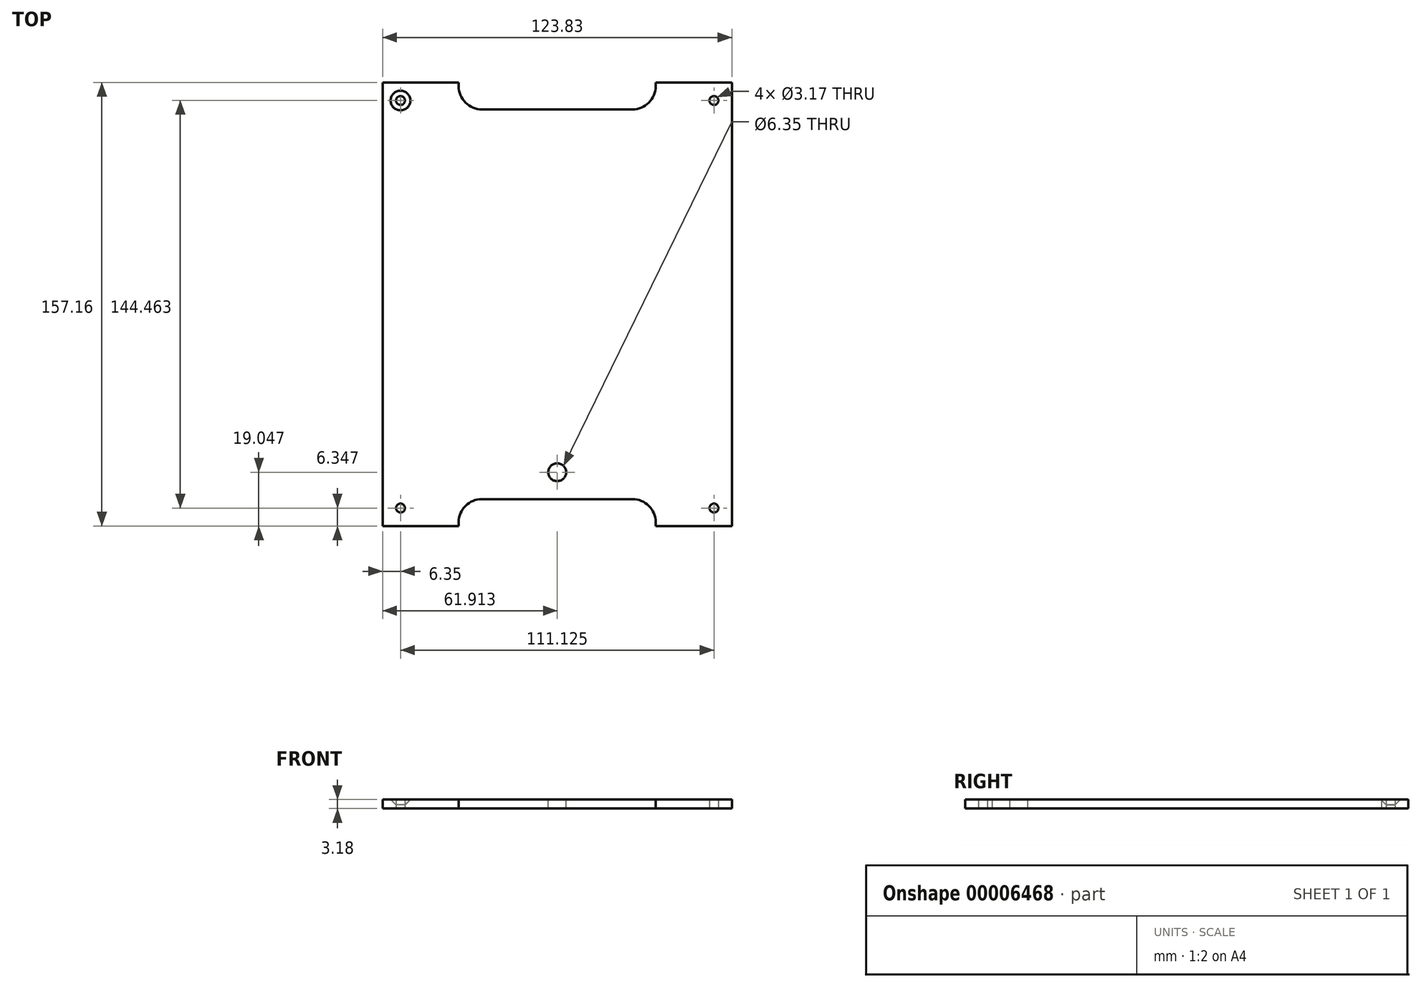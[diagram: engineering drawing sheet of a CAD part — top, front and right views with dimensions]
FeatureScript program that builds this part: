
annotation { "Feature Type Name" : "Feature", "Feature Type Description" : "" }
export const myFeature = defineFeature(function(context is Context, id is Id, definition is map)
    precondition{}
    {
        {
            var Q0;
            Q0=qCreatedBy(makeId("Top.planeOp"),FACE);
            var sketch = newSketch(context, id + "F0", { "sketchPlane" : qUnion([Q0])});
            skLineSegment(sketch, "E0.bottom", {"start": v(0, 0) * mm, "end": v(26.99, 0) * mm});
            skLineSegment(sketch, "E0.top", {"start": v(0, -157.16) * mm, "end": v(26.99, -157.16) * mm});
            skLineSegment(sketch, "E0.left", {"start": v(0, 0) * mm, "end": v(0, -157.16) * mm});
            skLineSegment(sketch, "E0.right", {"start": v(123.83, 0) * mm, "end": v(123.83, -157.16) * mm});
            skLineSegment(sketch, "E1", {"start": v(26.99, 0) * mm, "end": v(26.99, -1.27) * mm});
            skLineSegment(sketch, "E2", {"start": v(35.24, -9.53) * mm, "end": v(88.58, -9.53) * mm});
            skLineSegment(sketch, "E3", {"start": v(96.84, -1.27) * mm, "end": v(96.84, 0) * mm});
            skLineSegment(sketch, "E4", {"start": v(26.99, -157.16) * mm, "end": v(26.99, -155.9) * mm});
            skLineSegment(sketch, "E5", {"start": v(35.24, -147.64) * mm, "end": v(88.58, -147.64) * mm});
            skLineSegment(sketch, "E6", {"start": v(96.84, -155.9) * mm, "end": v(96.84, -157.16) * mm});
            skLineSegment(sketch, "E7.trimOffspring", {"start": v(96.84, 0) * mm, "end": v(123.83, 0) * mm});
            skLineSegment(sketch, "E8.trimOffspring", {"start": v(96.84, -157.16) * mm, "end": v(123.83, -157.16) * mm});
            skPoint(sketch, "E9.visualSharp", {"position": v(26.99, -9.53) * mm});
            skArc(sketch, "E9.filletArc", {"start": v(26.99, -1.27) * mm, "mid": v(29.4, -7.1) * mm, "end": v(35.24, -9.53) * mm});
            skPoint(sketch, "E10.visualSharp", {"position": v(96.84, -9.53) * mm});
            skArc(sketch, "E10.filletArc", {"start": v(88.58, -9.53) * mm, "mid": v(94.42, -7.1) * mm, "end": v(96.84, -1.27) * mm});
            skPoint(sketch, "E11.visualSharp", {"position": v(96.84, -147.64) * mm});
            skArc(sketch, "E11.filletArc", {"start": v(96.84, -155.9) * mm, "mid": v(94.42, -150.06) * mm, "end": v(88.58, -147.64) * mm});
            skPoint(sketch, "E12.visualSharp", {"position": v(26.99, -147.64) * mm});
            skArc(sketch, "E12.filletArc", {"start": v(35.24, -147.64) * mm, "mid": v(29.4, -150.06) * mm, "end": v(26.99, -155.9) * mm});
            skLineSegment(sketch, "E13.bottom", {"start": v(6.35, -6.35) * mm, "end": v(117.48, -6.35) * mm, "construction": true});
            skLineSegment(sketch, "E13.top", {"start": v(6.35, -150.81) * mm, "end": v(117.48, -150.81) * mm, "construction": true});
            skLineSegment(sketch, "E13.left", {"start": v(6.35, -6.35) * mm, "end": v(6.35, -150.81) * mm, "construction": true});
            skLineSegment(sketch, "E13.right", {"start": v(117.48, -6.35) * mm, "end": v(117.48, -150.81) * mm, "construction": true});
            skCircle(sketch, "E14", {"center": v(6.35, -6.35) * mm, "radius": 1.59 * mm});
            skCircle(sketch, "E15", {"center": v(117.48, -6.35) * mm, "radius": 1.59 * mm});
            skCircle(sketch, "E16", {"center": v(117.48, -150.81) * mm, "radius": 1.59 * mm});
            skCircle(sketch, "E17", {"center": v(6.35, -150.81) * mm, "radius": 1.59 * mm});
            skSolve(sketch);
        }
        {
            var Q0;
            Q0 = qSketchRegion(id + "F0", true);
            extrude(context, id + "F1", {"entities" : qUnion([Q0]), "depth" : 3.17 * mm});
        }
        {
            var Q0;
            Q0=qCreatedBy(makeId("Right.planeOp"),FACE);
            cPlane(context, id + "F2", {"entities" : qUnion([Q0]), "cplaneType" : CPlaneType.OFFSET, "offset" : 6.35 * mm, "width" : 152.4 * mm, "height" : 152.4 * mm});
        }
        {
            var Q0;
            Q0=qCreatedBy(id+"F2.planeOp",FACE);
            var sketch = newSketch(context, id + "F3", { "sketchPlane" : qUnion([Q0])});
            skLineSegment(sketch, "E18", {"start": v(-4.85, 0) * mm, "end": v(-4.85, 1.18) * mm});
            skLineSegment(sketch, "E19", {"start": v(-4.85, 1.18) * mm, "end": v(-2.85, 3.18) * mm});
            skLineSegment(sketch, "E20", {"start": v(-2.85, 3.18) * mm, "end": v(-6.35, 3.17) * mm});
            skLineSegment(sketch, "E21", {"start": v(-4.85, 0) * mm, "end": v(-6.35, 0) * mm});
            skLineSegment(sketch, "E22", {"start": v(-6.35, 3.17) * mm, "end": v(-6.35, 0) * mm});
            skSolve(sketch);
        }
        {
            var Q0;
            Q0 = qSketchRegion(id + "F3", true);
            var Q1;
            Q1=sQuery(id+"F3.wireOp",EDGE,"E22");
            revolve(context, id + "F4", {"operationType" : NewBodyOperationType.REMOVE, "entities" : qUnion([Q0]), "axis" : qUnion([Q1]), "revolveType" : RevolveType.FULL, "oppositeDirection" : true});
        }
        {
            var Q0;
            Q0=makeQuery(id+"F1.opExtrude","CAP_FACE",FACE,{"disambiguationData":[OSD([sQuery(id+"F0.wireOp",EDGE,"E0.bottom"),sQuery(id+"F0.wireOp",EDGE,"E0.top"),sQuery(id+"F0.wireOp",EDGE,"E0.left"),sQuery(id+"F0.wireOp",EDGE,"E0.right"),sQuery(id+"F0.wireOp",EDGE,"E1"),sQuery(id+"F0.wireOp",EDGE,"E2"),sQuery(id+"F0.wireOp",EDGE,"E3"),sQuery(id+"F0.wireOp",EDGE,"E4"),sQuery(id+"F0.wireOp",EDGE,"E5"),sQuery(id+"F0.wireOp",EDGE,"E6"),sQuery(id+"F0.wireOp",EDGE,"E7.trimOffspring"),sQuery(id+"F0.wireOp",EDGE,"E8.trimOffspring"),sQuery(id+"F0.wireOp",EDGE,"E9.filletArc"),sQuery(id+"F0.wireOp",EDGE,"E10.filletArc"),sQuery(id+"F0.wireOp",EDGE,"E11.filletArc"),sQuery(id+"F0.wireOp",EDGE,"E12.filletArc"),sQuery(id+"F0.wireOp",EDGE,"E14"),sQuery(id+"F0.wireOp",EDGE,"E15"),sQuery(id+"F0.wireOp",EDGE,"E16"),sQuery(id+"F0.wireOp",EDGE,"E17")])],"isStart":false});
            var sketch = newSketch(context, id + "F5", { "sketchPlane" : qUnion([Q0])});
            skCircle(sketch, "E23", {"center": v(61.91, -138.11) * mm, "radius": 3.18 * mm});
            skLineSegment(sketch, "E24", {"start": v(61.91, -138.11) * mm, "end": v(61.91, -147.64) * mm, "construction": true});
            skSolve(sketch);
        }
        {
            var Q0;
            Q0 = qSketchRegion(id + "F5", true);
            extrude(context, id + "F6", {"entities" : qUnion([Q0]), "operationType" : NewBodyOperationType.REMOVE, "endBound" : BoundingType.THROUGH_ALL, "oppositeDirection" : true, "depth" : 25.4 * mm});
        }
    });
